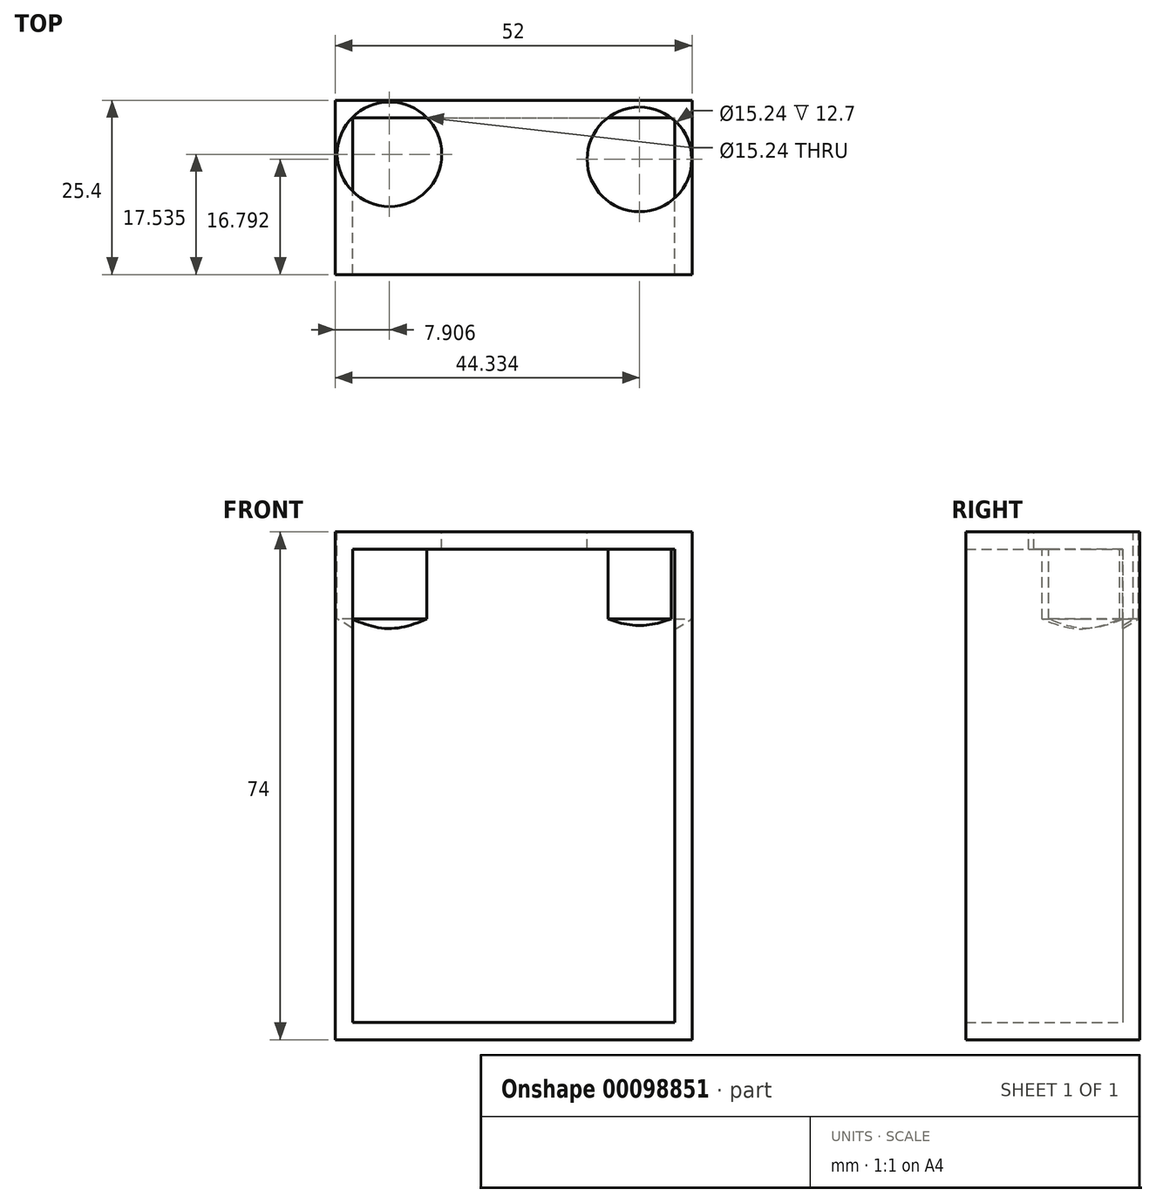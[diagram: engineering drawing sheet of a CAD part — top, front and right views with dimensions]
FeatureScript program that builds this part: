
annotation { "Feature Type Name" : "Feature", "Feature Type Description" : "" }
export const myFeature = defineFeature(function(context is Context, id is Id, definition is map)
    precondition{}
    {
        {
            var Q0;
            Q0=qCreatedBy(makeId("Front.planeOp"),FACE);
            var sketch = newSketch(context, id + "F0", { "sketchPlane" : qUnion([Q0])});
            skLineSegment(sketch, "E0.bottom", {"start": v(-26, 37) * mm, "end": v(26, 37) * mm});
            skLineSegment(sketch, "E0.top", {"start": v(-26, -37) * mm, "end": v(26, -37) * mm});
            skLineSegment(sketch, "E0.left", {"start": v(-26, 37) * mm, "end": v(-26, -37) * mm});
            skLineSegment(sketch, "E0.right", {"start": v(26, 37) * mm, "end": v(26, -37) * mm});
            skPoint(sketch, "E0.middle", {"position": v(0, 0) * mm});
            skSolve(sketch);
        }
        {
            var Q0;
            Q0=makeQuery(id+"F0.imprint","IMPRINT",FACE,{"disambiguationData":[TD([[makeQuery(id+"F0.imprint","IMPRINT",EDGE,{"derivedFrom":sQuery(id+"F0.wireOp",EDGE,"E0.bottom")}),-1.0]])]});
            extrude(context, id + "F1", {"entities" : qUnion([Q0]), "depth" : 25.4 * mm});
        }
        {
            var Q0;
            Q0=makeQuery(id+"F1.opExtrude","CAP_FACE",FACE,{"disambiguationData":[OSD([sQuery(id+"F0.wireOp",EDGE,"E0.bottom"),sQuery(id+"F0.wireOp",EDGE,"E0.top"),sQuery(id+"F0.wireOp",EDGE,"E0.left"),sQuery(id+"F0.wireOp",EDGE,"E0.right")])],"isStart":false});
            shell(context, id + "F2", {"entities" : qUnion([Q0]), "thickness" : 2.54 * mm});
        }
        {
            var Q0;
            Q0=makeQuery(id+"F1.opExtrude","SWEPT_FACE",FACE,{"disambiguationData":[OSD([sQuery(id+"F0.wireOp",EDGE,"E0.bottom")])]});
            var sketch = newSketch(context, id + "F3", { "sketchPlane" : qUnion([Q0])});
            skPoint(sketch, "E1", {"position": v(-18.1, -7.86) * mm});
            skPoint(sketch, "E2", {"position": v(18.33, -8.6) * mm});
            skSolve(sketch);
        }
        {
            var Q0;
            Q0=sQuery(id+"F3.wireOp",VERTEX,"E1");
            var Q1;
            Q1=sQuery(id+"F3.wireOp",VERTEX,"E2");
            var Q2;
            Q2=makeQuery(id+"F1.opExtrude","SWEPT_BODY",BODY,{"disambiguationData":[OSD([sQuery(id+"F0.wireOp",EDGE,"E0.bottom"),sQuery(id+"F0.wireOp",EDGE,"E0.top"),sQuery(id+"F0.wireOp",EDGE,"E0.left"),sQuery(id+"F0.wireOp",EDGE,"E0.right")])]});
            hole(context, id + "F4", {"style" : HoleStyle.SIMPLE, "endStyle" : HoleEndStyle.BLIND, "holeDiameter" : 15.24 * mm, "holeDepth" : 12.7 * mm, "locations" : qUnion([Q0, Q1]), "scope" : qUnion([Q2])});
        }
    });
